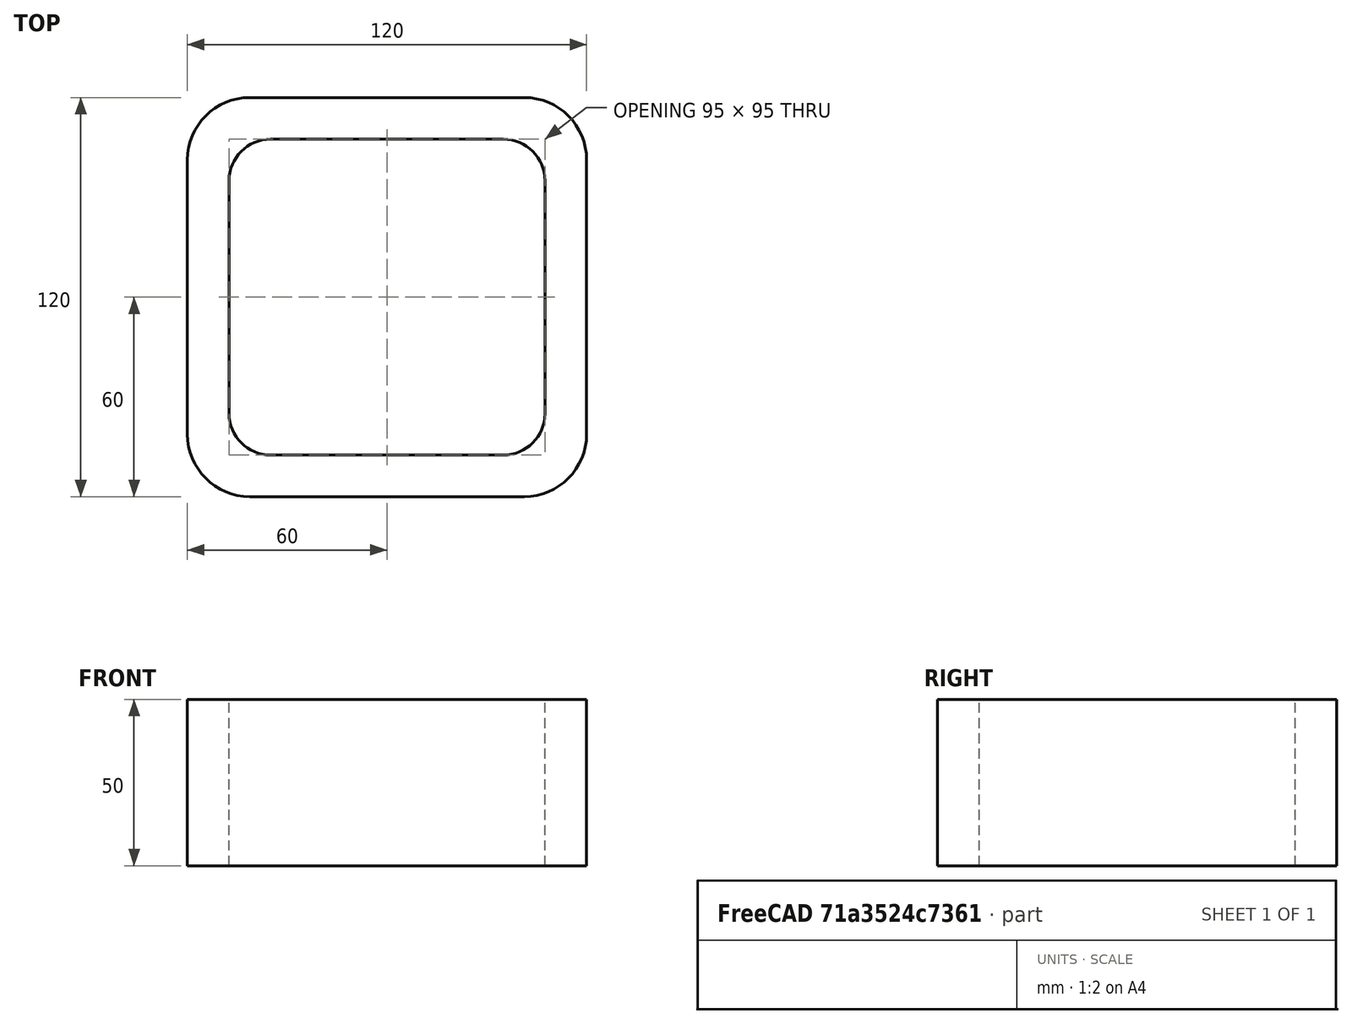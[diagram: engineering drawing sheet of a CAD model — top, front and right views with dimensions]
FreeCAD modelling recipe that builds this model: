
FCSTD DOCUMENT  (FreeCAD 0.15R4671 (Git))
Label: Square hollow section 120x120x12.5 EN10219 S235JRH
License: All rights reserved
LicenseURL: http://en.wikipedia.org/wiki/All_rights_reserved
objects: Sketcher::SketchObject×1, Part::Extrusion×1
note: 2 computed .brp shape members not serialized (recipe doc carries the construction recipe); baked Part::Feature solids carry a one-line shape summary decoded from their .brp

FEATURE [Sketcher::SketchObject] Sketch
  sketch-geometry (16):
    g0: LineSegment StartX=-35 StartY=47.5 StartZ=0 EndX=35 EndY=47.5 EndZ=0
    g1: LineSegment StartX=47.5 StartY=35 StartZ=0 EndX=47.5 EndY=-35 EndZ=0
    g2: LineSegment StartX=35 StartY=-47.5 StartZ=0 EndX=-35 EndY=-47.5 EndZ=0
    g3: LineSegment StartX=-47.5 StartY=-35 StartZ=0 EndX=-47.5 EndY=35 EndZ=0
    g4: LineSegment StartX=-41.25 StartY=60 StartZ=0 EndX=41.25 EndY=60 EndZ=0
    g5: LineSegment StartX=60 StartY=41.25 StartZ=0 EndX=60 EndY=-41.25 EndZ=0
    g6: LineSegment StartX=41.25 StartY=-60 StartZ=0 EndX=-41.25 EndY=-60 EndZ=0
    g7: LineSegment StartX=-60 StartY=-41.25 StartZ=0 EndX=-60 EndY=41.25 EndZ=0
    g8: ArcOfCircle CenterX=-35 CenterY=35 CenterZ=0 NormalX=0 NormalY=0 NormalZ=1 Radius=12.5 StartAngle=1.5708 EndAngle=3.14159
    g9: ArcOfCircle CenterX=35 CenterY=35 CenterZ=0 NormalX=0 NormalY=0 NormalZ=1 Radius=12.5 StartAngle=0 EndAngle=1.5708
    g10: ArcOfCircle CenterX=35 CenterY=-35 CenterZ=0 NormalX=0 NormalY=0 NormalZ=1 Radius=12.5 StartAngle=4.71239 EndAngle=6.28319
    g11: ArcOfCircle CenterX=-35 CenterY=-35 CenterZ=0 NormalX=0 NormalY=0 NormalZ=1 Radius=12.5 StartAngle=3.14159 EndAngle=4.71239
    g12: ArcOfCircle CenterX=41.25 CenterY=41.25 CenterZ=0 NormalX=0 NormalY=0 NormalZ=1 Radius=18.75 StartAngle=0 EndAngle=1.5708
    g13: ArcOfCircle CenterX=41.25 CenterY=-41.25 CenterZ=0 NormalX=0 NormalY=0 NormalZ=1 Radius=18.75 StartAngle=4.71239 EndAngle=6.28319
    g14: ArcOfCircle CenterX=-41.25 CenterY=-41.25 CenterZ=0 NormalX=0 NormalY=0 NormalZ=1 Radius=18.75 StartAngle=3.14159 EndAngle=4.71239
    g15: ArcOfCircle CenterX=-41.25 CenterY=41.25 CenterZ=0 NormalX=0 NormalY=0 NormalZ=1 Radius=18.75 StartAngle=1.5708 EndAngle=3.14159
  constraints (36):
    c: Horizontal(g2)
    c: Vertical(g3)
    c: Horizontal(g6)
    c: Vertical(g7)
    c: Tangent(g3,g8) = 1.5708
    c: Tangent(g0,g8) = 1.5708
    c: Tangent(g0,g9) = 1.5708
    c: Tangent(g1,g9) = 1.5708
    c: Tangent(g1,g10) = 1.5708
    c: Tangent(g2,g10) = 1.5708
    c: Tangent(g2,g11) = 1.5708
    c: Tangent(g3,g11) = 1.5708
    c: Tangent(g4,g12) = 1.5708
    c: Tangent(g5,g12) = 1.5708
    c: Tangent(g5,g13) = 1.5708
    c: Tangent(g6,g13) = 1.5708
    c: Tangent(g6,g14) = 1.5708
    c: Tangent(g7,g14) = 1.5708
    c: Tangent(g7,g15) = 1.5708
    c: Tangent(g4,g15) = 1.5708
    c: Equal(g9,g8)
    c: Equal(g9,g11)
    c: Equal(g9,g10)
    c: Equal(g12,g15)
    c: Equal(g12,g14)
    c: Equal(g12,g13)
    c: Symmetric(g4,g6,g-1)
    c: Symmetric(g7,g5,g-2)
    c: DistanceY(g4,g6) = -120
    c: DistanceX(g7,g5) = 120
    c: Symmetric(g3,g1,g-2)
    c: Symmetric(g0,g2,g-1)
    c: DistanceY(g0,g4) = 12.5
    c: DistanceX(g5,g1) = -12.5
    c: Radius(g9) = 12.5
    c: Radius(g12) = 18.75
FEATURE [Part::Extrusion] Extrude  label="Square hollow section 120x120x12.5 EN10219 S235JRH"
  Base = -> Sketch
  Dir = (0,0,50)
  Solid = true
